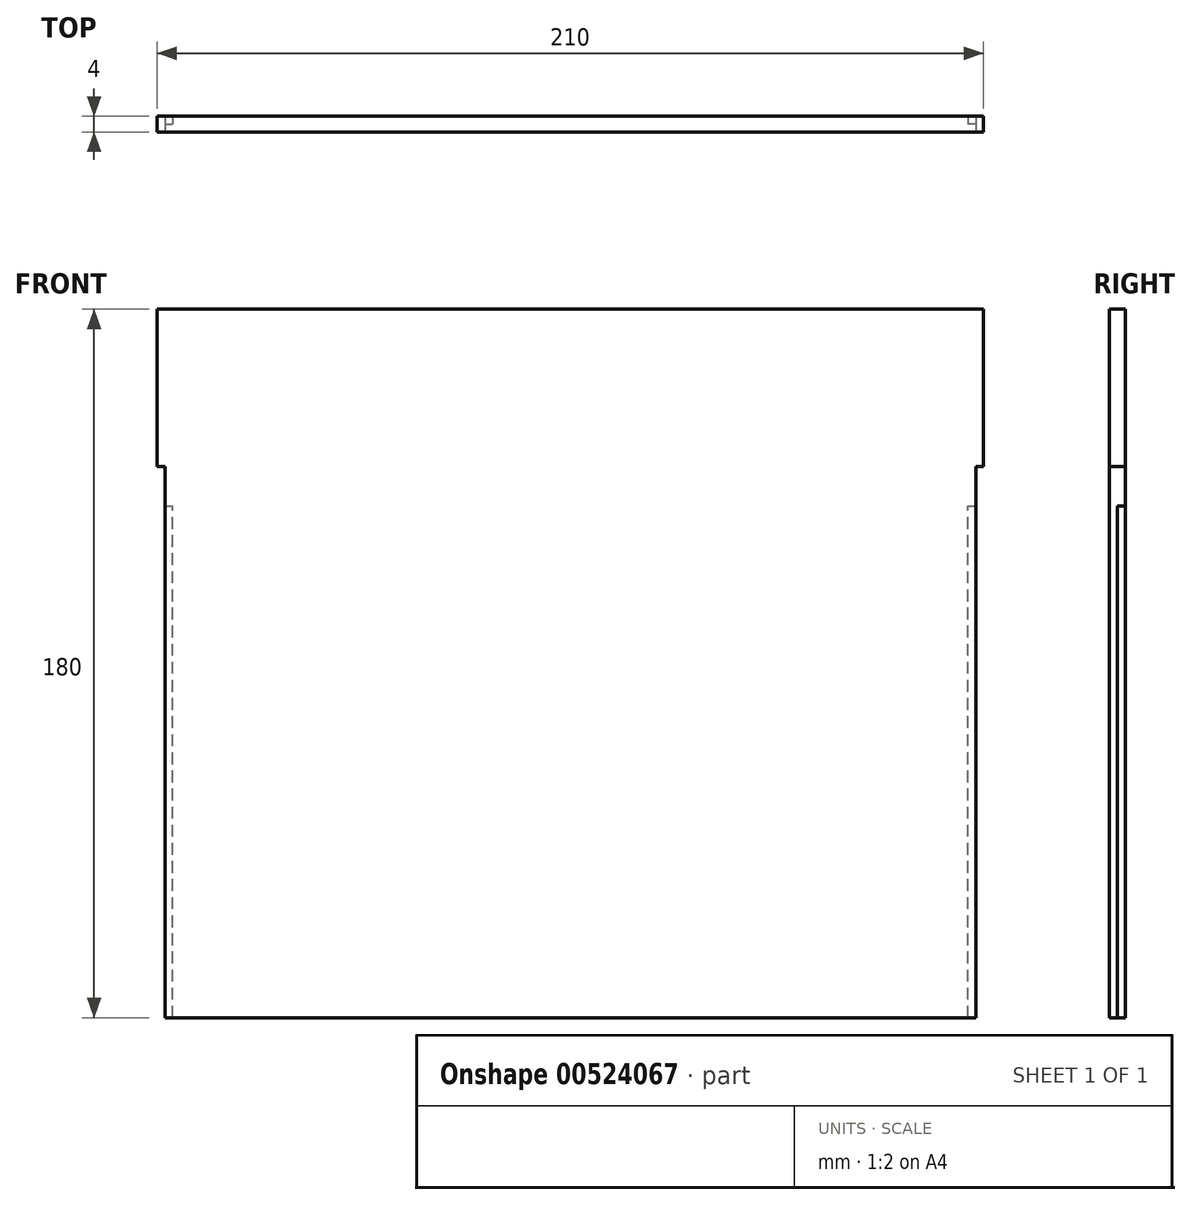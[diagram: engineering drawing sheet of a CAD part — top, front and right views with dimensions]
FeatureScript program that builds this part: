
annotation { "Feature Type Name" : "Feature", "Feature Type Description" : "" }
export const myFeature = defineFeature(function(context is Context, id is Id, definition is map)
    precondition{}
    {
        {
            var Q0;
            Q0=qCreatedBy(makeId("Front.planeOp"),FACE);
            var sketch = newSketch(context, id + "F0", { "sketchPlane" : qUnion([Q0])});
            skLineSegment(sketch, "E0.bottom", {"start": v(-86.61, 44.3) * mm, "end": v(123.39, 44.3) * mm});
            skLineSegment(sketch, "E0.top", {"start": v(-86.61, 4.3) * mm, "end": v(123.39, 4.3) * mm});
            skLineSegment(sketch, "E0.left", {"start": v(-86.61, 44.3) * mm, "end": v(-86.61, 4.3) * mm});
            skLineSegment(sketch, "E0.right", {"start": v(123.39, 44.3) * mm, "end": v(123.39, 4.3) * mm});
            skSolve(sketch);
        }
        {
            var Q0;
            Q0=makeQuery(id+"F0.imprint","IMPRINT",FACE,{"disambiguationData":[TD([[makeQuery(id+"F0.imprint","IMPRINT",EDGE,{"derivedFrom":sQuery(id+"F0.wireOp",EDGE,"E0.bottom")}),-1.0]])]});
            extrude(context, id + "F1", {"entities" : qUnion([Q0]), "depth" : 4 * mm, "offsetDistance" : 25 * mm});
        }
        {
            var Q0;
            Q0=makeQuery(id+"F1.opExtrude","SWEPT_FACE",FACE,{"disambiguationData":[OSD([sQuery(id+"F0.wireOp",EDGE,"E0.top")])]});
            var sketch = newSketch(context, id + "F2", { "sketchPlane" : qUnion([Q0])});
            skLineSegment(sketch, "E1.top", {"start": v(-84.6, 2) * mm, "end": v(-82.6, 2) * mm});
            skLineSegment(sketch, "E2.top", {"start": v(121.38, 2) * mm, "end": v(119.38, 2) * mm});
            skLineSegment(sketch, "E3.bottom", {"start": v(-82.6, 0) * mm, "end": v(119.38, 0) * mm});
            skLineSegment(sketch, "E3.top", {"start": v(-82.6, 4) * mm, "end": v(119.38, 4) * mm});
            skLineSegment(sketch, "E3.left", {"start": v(-82.6, 0) * mm, "end": v(-82.6, 4) * mm});
            skLineSegment(sketch, "E3.right", {"start": v(119.38, 0) * mm, "end": v(119.38, 4) * mm});
            skLineSegment(sketch, "E4.top", {"start": v(-84.6, 4) * mm, "end": v(-82.6, 4) * mm});
            skLineSegment(sketch, "E4.left", {"start": v(-84.6, 2) * mm, "end": v(-84.6, 4) * mm});
            skLineSegment(sketch, "E4.right", {"start": v(-82.6, 2) * mm, "end": v(-82.6, 4) * mm});
            skLineSegment(sketch, "E5.top", {"start": v(121.38, 4) * mm, "end": v(119.38, 4) * mm});
            skLineSegment(sketch, "E5.left", {"start": v(121.38, 2) * mm, "end": v(121.38, 4) * mm});
            skLineSegment(sketch, "E5.right", {"start": v(119.38, 2) * mm, "end": v(119.38, 4) * mm});
            skSolve(sketch);
        }
        {
            var Q0;
            Q0 = qSketchRegion(id + "F2", true);
            extrude(context, id + "F3", {"entities" : qUnion([Q0]), "operationType" : NewBodyOperationType.ADD, "depth" : 140 * mm, "offsetDistance" : 25 * mm});
        }
        {
            var Q0;
            {var subQ0=sQuery(id+"F0.wireOp",EDGE,"E0.right");var subQ2=sQuery(id+"F0.wireOp",EDGE,"E0.top");Q0=makeQuery(id+"F3.boolean.opBoolean","SPLIT",FACE,{"disambiguationData":[TD([makeQuery(id+"F1.opExtrude","SWEPT_FACE",FACE,{"disambiguationData":[OSD([subQ0])]})])],"derivedFrom":makeQuery(id+"F1.opExtrude","SWEPT_FACE",FACE,{"disambiguationData":[OSD([subQ2])]})});}
            var sketch = newSketch(context, id + "F4", { "sketchPlane" : qUnion([Q0])});
            skLineSegment(sketch, "E6.bottom", {"start": v(119.38, 0) * mm, "end": v(121.38, 0) * mm});
            skLineSegment(sketch, "E6.top", {"start": v(119.38, 2) * mm, "end": v(121.38, 2) * mm});
            skLineSegment(sketch, "E6.left", {"start": v(119.38, 0) * mm, "end": v(119.38, 2) * mm});
            skLineSegment(sketch, "E6.right", {"start": v(121.38, 0) * mm, "end": v(121.38, 2) * mm});
            skSolve(sketch);
        }
        {
            var Q0;
            Q0 = qSketchRegion(id + "F4", true);
            var Q1;
            Q1=makeQuery(id+"F4.imprint","IMPRINT",FACE,{"disambiguationData":[TD([[makeQuery(id+"F4.imprint","IMPRINT",EDGE,{"derivedFrom":sQuery(id+"F4.wireOp",EDGE,"E6.bottom")}),1.0]])]});
            extrude(context, id + "F5", {"entities" : qUnion([Q0, Q1]), "operationType" : NewBodyOperationType.ADD, "depth" : 10 * mm, "offsetDistance" : 25 * mm});
        }
        {
            var Q0;
            {var subQ1=sQuery(id+"F0.wireOp",EDGE,"E0.left");var subQ2=sQuery(id+"F0.wireOp",EDGE,"E0.top");Q0=makeQuery(id+"F3.boolean.opBoolean","SPLIT",FACE,{"disambiguationData":[TD([makeQuery(id+"F1.opExtrude","SWEPT_FACE",FACE,{"disambiguationData":[OSD([subQ1])]})])],"derivedFrom":makeQuery(id+"F1.opExtrude","SWEPT_FACE",FACE,{"disambiguationData":[OSD([subQ2])]})});}
            var sketch = newSketch(context, id + "F6", { "sketchPlane" : qUnion([Q0])});
            skLineSegment(sketch, "E7.bottom", {"start": v(-82.6, 0) * mm, "end": v(-84.6, 0) * mm});
            skLineSegment(sketch, "E7.top", {"start": v(-82.6, 2) * mm, "end": v(-84.6, 2) * mm});
            skLineSegment(sketch, "E7.left", {"start": v(-82.6, 0) * mm, "end": v(-82.6, 2) * mm});
            skLineSegment(sketch, "E7.right", {"start": v(-84.6, 0) * mm, "end": v(-84.6, 2) * mm});
            skSolve(sketch);
        }
        {
            var Q0;
            Q0=makeQuery(id+"F6.imprint","IMPRINT",FACE,{"disambiguationData":[TD([[makeQuery(id+"F6.imprint","IMPRINT",EDGE,{"derivedFrom":sQuery(id+"F6.wireOp",EDGE,"E7.bottom")}),1.0]])]});
            extrude(context, id + "F7", {"entities" : qUnion([Q0]), "operationType" : NewBodyOperationType.ADD, "depth" : 10 * mm, "offsetDistance" : 25 * mm});
        }
    });
